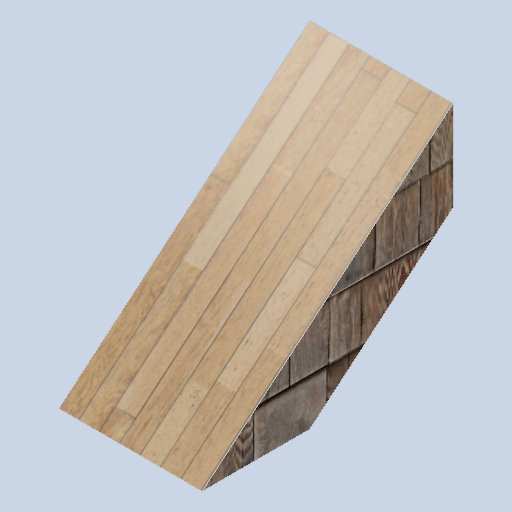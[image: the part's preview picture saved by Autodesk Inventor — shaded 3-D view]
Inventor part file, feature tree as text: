
AUTODESK INVENTOR PART (.ipt)
format: ipt  version: 2024.2 (Build 282272000, 272)  size: 304,128 bytes
history: native  units: in
note: dims shown in document units (in); Inventor stores cm internally (conversion verified against a paired STEP export)
features: other x3, sketch x1
ambient origin geometry x8: Origin, YZ Plane, XZ Plane, XY Plane, X Axis, Y Axis, Z Axis, Center Point
bodies: Body1 (feature_tree)
feature tree (4):
  other  "frame_rib_01.ipt"
  other  "Solid3::frame_rib_01.ipt"
  other  "TaggingFeature1"
  sketch  "Sketch1"  dims[d0=0.3937in]
